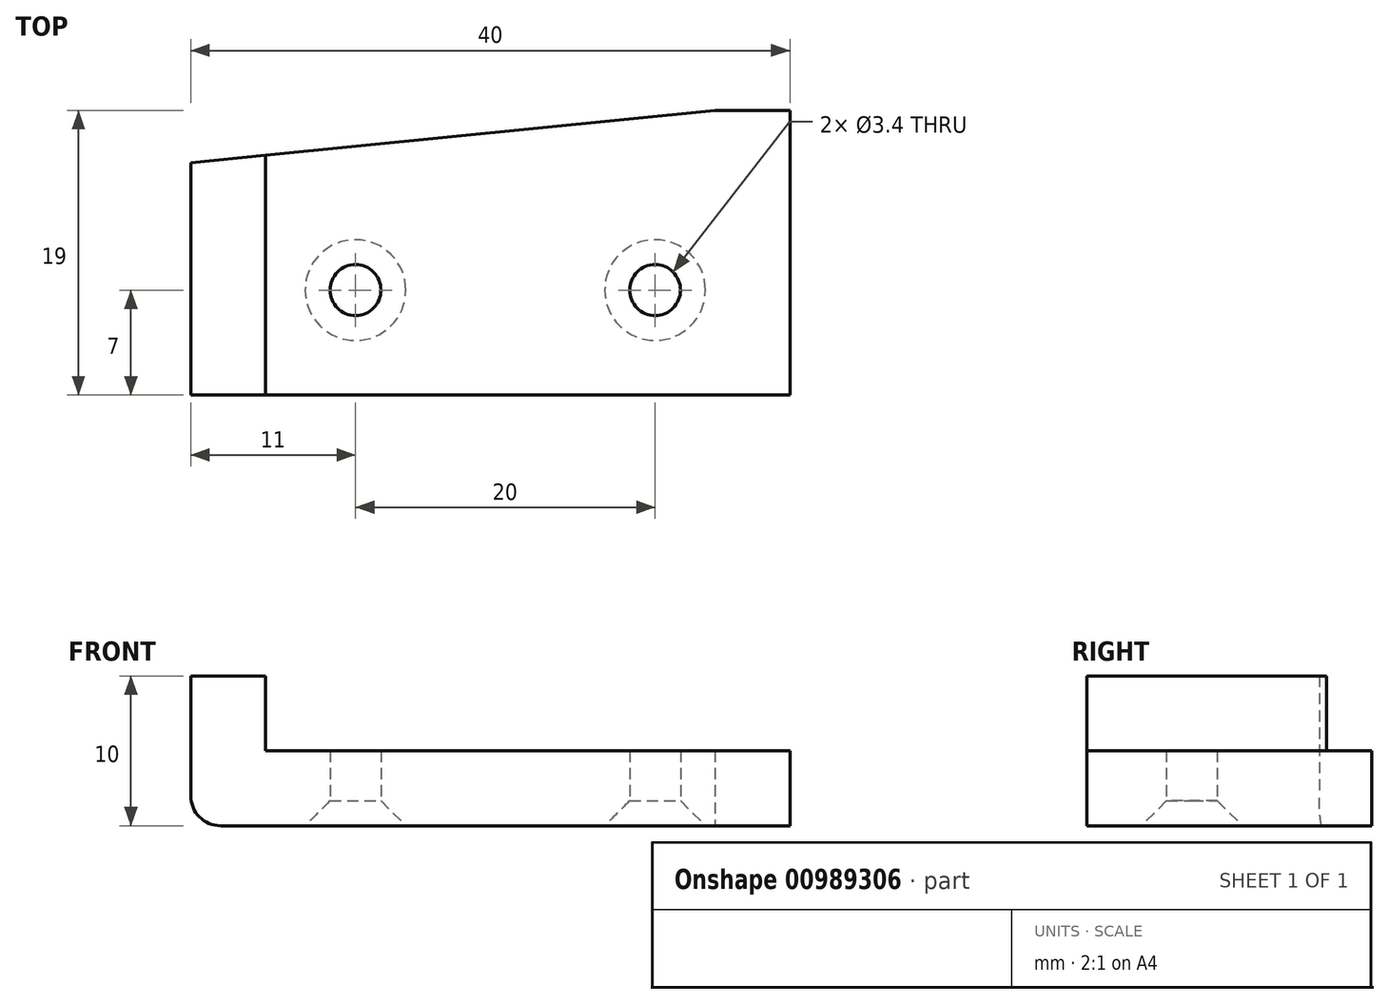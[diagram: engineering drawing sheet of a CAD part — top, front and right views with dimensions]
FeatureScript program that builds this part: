
annotation { "Feature Type Name" : "Feature", "Feature Type Description" : "" }
export const myFeature = defineFeature(function(context is Context, id is Id, definition is map)
    precondition{}
    {
        {
            var Q0;
            Q0=qCreatedBy(makeId("Front.planeOp"),FACE);
            var sketch = newSketch(context, id + "F0", { "sketchPlane" : qUnion([Q0])});
            skLineSegment(sketch, "E0", {"start": v(0, 0) * mm, "end": v(-40, 0) * mm});
            skLineSegment(sketch, "E1", {"start": v(-40, 0) * mm, "end": v(-40, 10) * mm});
            skLineSegment(sketch, "E2", {"start": v(-35, 10) * mm, "end": v(-40, 10) * mm});
            skLineSegment(sketch, "E3", {"start": v(-35, 10) * mm, "end": v(-35, 5) * mm});
            skLineSegment(sketch, "E4", {"start": v(-35, 5) * mm, "end": v(0, 5) * mm});
            skLineSegment(sketch, "E5", {"start": v(0, 0) * mm, "end": v(0, 5) * mm});
            skSolve(sketch);
        }
        {
            var Q0;
            Q0=makeQuery(id+"F0.imprint","IMPRINT",FACE,{"disambiguationData":[TD([[makeQuery(id+"F0.imprint","IMPRINT",EDGE,{"derivedFrom":sQuery(id+"F0.wireOp",EDGE,"E0")}),-1.0]])]});
            extrude(context, id + "F1", {"entities" : qUnion([Q0]), "depth" : 19 * mm, "offsetDistance" : 25 * mm});
        }
        {
            var Q0;
            Q0=makeQuery(id+"F1.opExtrude","SWEPT_FACE",FACE,{"disambiguationData":[OSD([sQuery(id+"F0.wireOp",EDGE,"E0")])]});
            var sketch = newSketch(context, id + "F2", { "sketchPlane" : qUnion([Q0])});
            skPoint(sketch, "E6", {"position": v(-9, 12) * mm});
            skPoint(sketch, "E7", {"position": v(-29, 12) * mm});
            skPoint(sketch, "E8", {"position": v(-5, 0) * mm});
            skPoint(sketch, "E9", {"position": v(-40, 3.5) * mm});
            skLineSegment(sketch, "E10", {"start": v(-40, 3.5) * mm, "end": v(-5, 0) * mm});
            skLineSegment(sketch, "E11", {"start": v(-40, 0) * mm, "end": v(-40, 3.5) * mm});
            skLineSegment(sketch, "E12", {"start": v(-40, 0) * mm, "end": v(-5, 0) * mm});
            skSolve(sketch);
        }
        {
            var Q0;
            Q0 = qSketchRegion(id + "F2", true);
            extrude(context, id + "F3", {"entities" : qUnion([Q0]), "operationType" : NewBodyOperationType.REMOVE, "oppositeDirection" : true, "depth" : 25 * mm, "offsetDistance" : 25 * mm});
        }
        {
            var Q0;
            Q0=sQuery(id+"F2.wireOp",VERTEX,"E6");
            var Q1;
            Q1=sQuery(id+"F2.wireOp",VERTEX,"E7");
            var Q2;
            Q2=makeQuery(id+"F1.opExtrude","SWEPT_BODY",BODY,{"disambiguationData":[OSD([sQuery(id+"F0.wireOp",EDGE,"E0"),sQuery(id+"F0.wireOp",EDGE,"E1"),sQuery(id+"F0.wireOp",EDGE,"E2"),sQuery(id+"F0.wireOp",EDGE,"E3"),sQuery(id+"F0.wireOp",EDGE,"E4"),sQuery(id+"F0.wireOp",EDGE,"E5")])]});
            hole(context, id + "F4", {"style" : HoleStyle.C_SINK, "endStyle" : HoleEndStyle.THROUGH, "standardTappedOrClearance" : lookupTablePath({ "fit" : "Normal", "standard" : "ISO", "size" : "M3", "type" : "Clearance" }), "standardBlindInLast" : lookupTablePath({ "fit" : "Normal", "standard" : "ISO", "engagement" : "75%", "pitch" : "0.5 mm", "size" : "M3", "type" : "Clearance & tapped" }), "holeDiameter" : 3.4 * mm, "cSinkDiameter" : 6.72 * mm, "cSinkAngle" : 90 * degree, "majorDiameter" : 5 * mm, "isTappedThrough" : true, "tappedDepth" : 5.6 * mm, "tapClearance" : 3, "startFromSketch" : true, "locations" : qUnion([Q0, Q1]), "scope" : qUnion([Q2])});
        }
        {
            var Q0;
            Q0=makeQuery(id+"F1.opExtrude","SWEPT_EDGE",EDGE,{"disambiguationData":[OSD([sQuery(id+"F0.wireOp",EDGE,"E0"),sQuery(id+"F0.wireOp",EDGE,"E1")])]});
            fillet(context, id + "F5", {"entities" : qUnion([Q0]), "radius" : 2 * mm, "tangentPropagation" : true, "allowEdgeOverflow" : false});
        }
    });
